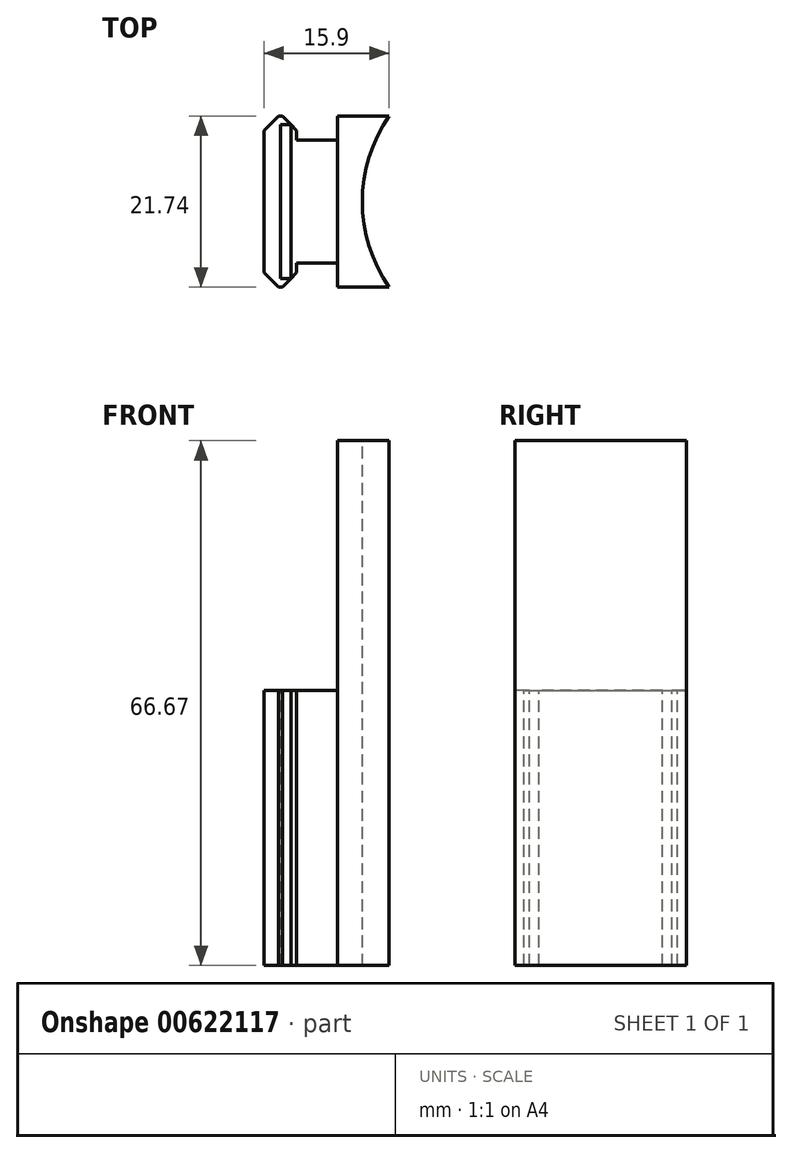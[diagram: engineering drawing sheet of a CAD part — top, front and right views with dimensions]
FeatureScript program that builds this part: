
annotation { "Feature Type Name" : "Feature", "Feature Type Description" : "" }
export const myFeature = defineFeature(function(context is Context, id is Id, definition is map)
    precondition{}
    {
        {
            var Q0;
            Q0=qCreatedBy(makeId("Top.planeOp"),FACE);
            var sketch = newSketch(context, id + "F0", { "sketchPlane" : qUnion([Q0])});
            skLineSegment(sketch, "E0", {"start": v(0, 22.6) * mm, "end": v(0, -22.6) * mm});
            skLineSegment(sketch, "E1", {"start": v(0, 0) * mm, "end": v(-7.34, 0) * mm});
            skPoint(sketch, "E1.endSnap0", {"position": v(0, 0) * mm});
            skPoint(sketch, "E2", {"position": v(-7.24, 0) * mm});
            skLineSegment(sketch, "E3.bottom", {"start": v(-9.32, -9.75) * mm, "end": v(-5.16, -9.75) * mm});
            skLineSegment(sketch, "E3.top", {"start": v(-9.32, 9.75) * mm, "end": v(-5.16, 9.75) * mm});
            skLineSegment(sketch, "E3.left", {"start": v(-9.32, -9.75) * mm, "end": v(-9.32, 9.75) * mm});
            skLineSegment(sketch, "E3.right", {"start": v(-5.16, -9.75) * mm, "end": v(-5.16, 9.75) * mm});
            skLineSegment(sketch, "E4", {"start": v(-5.16, 7.82) * mm, "end": v(0, 7.82) * mm});
            skLineSegment(sketch, "E5.MirrorCS", {"start": v(-5.16, -7.82) * mm, "end": v(0, -7.82) * mm});
            skLineSegment(sketch, "E6", {"start": v(0, 10.87) * mm, "end": v(-12.73, 10.87) * mm});
            skLineSegment(sketch, "E7.MirrorCS", {"start": v(0, -10.87) * mm, "end": v(-12.73, -10.87) * mm});
            skLineSegment(sketch, "E8", {"start": v(-7.24, -19.08) * mm, "end": v(-7.24, 22.23) * mm});
            skPoint(sketch, "E8.startSnap0", {"position": v(-7.24, -9.75) * mm});
            skLineSegment(sketch, "E9", {"start": v(-8.61, -16.87) * mm, "end": v(-8.61, 22.8) * mm});
            skLineSegment(sketch, "E10.MirrorCS", {"start": v(-5.87, -16.87) * mm, "end": v(-5.87, 22.8) * mm});
            skLineSegment(sketch, "E11", {"start": v(-8.61, 9.75) * mm, "end": v(-7.24, 11.13) * mm});
            skPoint(sketch, "E11.endSnap0", {"position": v(-6.36, -10.87) * mm});
            skLineSegment(sketch, "E12", {"start": v(-5.87, 9.75) * mm, "end": v(-7.24, 11.13) * mm});
            skLineSegment(sketch, "E13.MirrorCS", {"start": v(-8.61, -9.75) * mm, "end": v(-6.68, -11.69) * mm});
            skLineSegment(sketch, "E14.MirrorCS", {"start": v(-5.87, -9.75) * mm, "end": v(-7.24, -11.13) * mm});
            skLineSegment(sketch, "E15", {"start": v(-5.87, 9.75) * mm, "end": v(-5.16, 9.04) * mm});
            skLineSegment(sketch, "E16.MirrorCS", {"start": v(-8.61, 9.75) * mm, "end": v(-9.32, 9.04) * mm});
            skLineSegment(sketch, "E17.MirrorCS", {"start": v(-14.48, 0) * mm, "end": v(-7.14, 0) * mm});
            skLineSegment(sketch, "E18.MirrorCS", {"start": v(-8.61, -9.75) * mm, "end": v(-9.32, -9.04) * mm});
            skLineSegment(sketch, "E19.MirrorCS", {"start": v(-5.87, -9.75) * mm, "end": v(-5.16, -9.04) * mm});
            skCircle(sketch, "E20", {"center": v(22.23, 0) * mm, "radius": 19.05 * mm});
            skLineSegment(sketch, "E21", {"start": v(0, -10.87) * mm, "end": v(6.58, -10.87) * mm});
            skLineSegment(sketch, "E22", {"start": v(0, 10.87) * mm, "end": v(6.58, 10.87) * mm});
            skLineSegment(sketch, "E23", {"start": v(6.58, -10.87) * mm, "end": v(6.58, 10.87) * mm});
            skCircle(sketch, "E24", {"center": v(22.23, 0) * mm, "radius": 22.23 * mm});
            skSolve(sketch);
        }
        {
            var Q0;
            {var subQ4=sQuery(id+"F0.wireOp",EDGE,"E21");Q0=makeQuery(id+"F0.imprint","IMPRINT",FACE,{"disambiguationData":[TD([[makeQuery(id+"F0.imprint","IMPRINT",EDGE,{"derivedFrom":subQ4}),1.0]])]});}
            var Q1;
            {var subQ2=sQuery(id+"F0.wireOp",EDGE,"E22");Q1=makeQuery(id+"F0.imprint","IMPRINT",FACE,{"disambiguationData":[TD([[makeQuery(id+"F0.imprint","IMPRINT",EDGE,{"derivedFrom":subQ2}),-1.0]])]});}
            var Q2;
            {var subQ3=sQuery(id+"F0.wireOp",EDGE,"E4");Q2=makeQuery(id+"F0.imprint","IMPRINT",FACE,{"disambiguationData":[TD([[makeQuery(id+"F0.imprint","IMPRINT",EDGE,{"derivedFrom":subQ3}),-1.0]])]});}
            var Q3;
            {var subQ3=sQuery(id+"F0.wireOp",EDGE,"E5.MirrorCS");Q3=makeQuery(id+"F0.imprint","IMPRINT",FACE,{"disambiguationData":[TD([[makeQuery(id+"F0.imprint","IMPRINT",EDGE,{"derivedFrom":subQ3}),1.0]])]});}
            var Q4;
            {var subQ3=sQuery(id+"F0.wireOp",EDGE,"E1");var subQ7=sQuery(id+"F0.wireOp",EDGE,"E17.MirrorCS");var subQ9=makeQuery(id+"F0.imprint","INTERSECT",VERTEX,{"derivedFrom":[subQ3,subQ7]});Q4=makeQuery(id+"F0.imprint","IMPRINT",FACE,{"disambiguationData":[TD([[makeQuery(id+"F0.imprint","IMPRINT",EDGE,{"disambiguationData":[TD([[subQ9,1.0]])],"derivedFrom":subQ3}),1.0]])]});}
            var Q5;
            {var subQ0=sQuery(id+"F0.wireOp",EDGE,"E14.MirrorCS");var subQ5=sQuery(id+"F0.wireOp",EDGE,"E7.MirrorCS");var subQ6=makeQuery(id+"F0.imprint","INTERSECT",VERTEX,{"derivedFrom":[subQ5,subQ0]});Q5=makeQuery(id+"F0.imprint","IMPRINT",FACE,{"disambiguationData":[TD([[makeQuery(id+"F0.imprint","IMPRINT",EDGE,{"disambiguationData":[TD([[subQ6,-1.0]])],"derivedFrom":subQ5}),-1.0]])]});}
            var Q6;
            {var subQ0=sQuery(id+"F0.wireOp",EDGE,"E13.MirrorCS");var subQ5=sQuery(id+"F0.wireOp",EDGE,"E7.MirrorCS");var subQ7=makeQuery(id+"F0.imprint","INTERSECT",VERTEX,{"derivedFrom":[subQ5,subQ0]});Q6=makeQuery(id+"F0.imprint","IMPRINT",FACE,{"disambiguationData":[TD([[makeQuery(id+"F0.imprint","IMPRINT",EDGE,{"disambiguationData":[TD([[subQ7,1.0]])],"derivedFrom":subQ5}),-1.0]])]});}
            var Q7;
            {var subQ0=sQuery(id+"F0.wireOp",EDGE,"E17.MirrorCS");var subQ1=makeQuery(id+"F0.imprint","IMPRINT",VERTEX,{"derivedFrom":subQ0});Q7=makeQuery(id+"F0.imprint","IMPRINT",FACE,{"disambiguationData":[TD([[makeQuery(id+"F0.imprint","IMPRINT",EDGE,{"disambiguationData":[TD([[subQ1,1.0]])],"derivedFrom":subQ0}),-1.0]])]});}
            var Q8;
            {var subQ0=sQuery(id+"F0.wireOp",EDGE,"E19.MirrorCS");Q8=makeQuery(id+"F0.imprint","IMPRINT",FACE,{"disambiguationData":[TD([[makeQuery(id+"F0.imprint","IMPRINT",EDGE,{"derivedFrom":subQ0}),1.0]])]});}
            var Q9;
            {var subQ0=sQuery(id+"F0.wireOp",EDGE,"E15");Q9=makeQuery(id+"F0.imprint","IMPRINT",FACE,{"disambiguationData":[TD([[makeQuery(id+"F0.imprint","IMPRINT",EDGE,{"derivedFrom":subQ0}),-1.0]])]});}
            var Q10;
            {var subQ3=sQuery(id+"F0.wireOp",EDGE,"E1");var subQ7=sQuery(id+"F0.wireOp",EDGE,"E17.MirrorCS");var subQ9=makeQuery(id+"F0.imprint","INTERSECT",VERTEX,{"derivedFrom":[subQ3,subQ7]});Q10=makeQuery(id+"F0.imprint","IMPRINT",FACE,{"disambiguationData":[TD([[makeQuery(id+"F0.imprint","IMPRINT",EDGE,{"disambiguationData":[TD([[subQ9,1.0]])],"derivedFrom":subQ3}),-1.0]])]});}
            var Q11;
            {var subQ0=sQuery(id+"F0.wireOp",EDGE,"E17.MirrorCS");var subQ1=makeQuery(id+"F0.imprint","IMPRINT",VERTEX,{"derivedFrom":subQ0});Q11=makeQuery(id+"F0.imprint","IMPRINT",FACE,{"disambiguationData":[TD([[makeQuery(id+"F0.imprint","IMPRINT",EDGE,{"disambiguationData":[TD([[subQ1,1.0]])],"derivedFrom":subQ0}),1.0]])]});}
            var Q12;
            {var subQ0=sQuery(id+"F0.wireOp",EDGE,"E16.MirrorCS");Q12=makeQuery(id+"F0.imprint","IMPRINT",FACE,{"disambiguationData":[TD([[makeQuery(id+"F0.imprint","IMPRINT",EDGE,{"derivedFrom":subQ0}),1.0]])]});}
            var Q13;
            {var subQ0=sQuery(id+"F0.wireOp",EDGE,"E18.MirrorCS");Q13=makeQuery(id+"F0.imprint","IMPRINT",FACE,{"disambiguationData":[TD([[makeQuery(id+"F0.imprint","IMPRINT",EDGE,{"derivedFrom":subQ0}),-1.0]])]});}
            var Q14;
            {var subQ0=sQuery(id+"F0.wireOp",EDGE,"E12");var subQ5=sQuery(id+"F0.wireOp",EDGE,"E6");var subQ6=makeQuery(id+"F0.imprint","INTERSECT",VERTEX,{"derivedFrom":[subQ5,subQ0]});Q14=makeQuery(id+"F0.imprint","IMPRINT",FACE,{"disambiguationData":[TD([[makeQuery(id+"F0.imprint","IMPRINT",EDGE,{"disambiguationData":[TD([[subQ6,-1.0]])],"derivedFrom":subQ5}),1.0]])]});}
            var Q15;
            {var subQ0=sQuery(id+"F0.wireOp",EDGE,"E11");var subQ5=sQuery(id+"F0.wireOp",EDGE,"E6");var subQ6=makeQuery(id+"F0.imprint","INTERSECT",VERTEX,{"derivedFrom":[subQ5,subQ0]});Q15=makeQuery(id+"F0.imprint","IMPRINT",FACE,{"disambiguationData":[TD([[makeQuery(id+"F0.imprint","IMPRINT",EDGE,{"disambiguationData":[TD([[subQ6,1.0]])],"derivedFrom":subQ5}),1.0]])]});}
            var Q16;
            {var subQ0=sQuery(id+"F0.wireOp",EDGE,"E24");var subQ5=sQuery(id+"F0.wireOp",EDGE,"E21");var subQ8=makeQuery(id+"F0.imprint","INTERSECT",VERTEX,{"derivedFrom":[subQ5,subQ0]});Q16=makeQuery(id+"F0.imprint","IMPRINT",FACE,{"disambiguationData":[TD([[makeQuery(id+"F0.imprint","IMPRINT",EDGE,{"disambiguationData":[TD([[subQ8,-1.0]])],"derivedFrom":subQ5}),1.0]])]});}
            extrude(context, id + "F1", {"entities" : qUnion([Q0, Q1, Q2, Q3, Q4, Q5, Q6, Q7, Q8, Q9, Q10, Q11, Q12, Q13, Q14, Q15, Q16]), "oppositeDirection" : true, "depth" : 34.92 * mm, "offsetDistance" : 25.4 * mm});
        }
        {
            var Q0;
            {var subQ0=sQuery(id+"F0.wireOp",EDGE,"E0");var subQ1=makeQuery(id+"F0.imprint","INTERSECT",VERTEX,{"derivedFrom":[subQ0,sQuery(id+"F0.wireOp",EDGE,"E4")]});Q0=makeQuery(id+"F0.imprint","IMPRINT",FACE,{"disambiguationData":[TD([[makeQuery(id+"F0.imprint","IMPRINT",EDGE,{"disambiguationData":[TD([[subQ1,1.0]])],"derivedFrom":subQ0}),1.0]])]});}
            var Q1;
            {var subQ1=sQuery(id+"F0.wireOp",EDGE,"E0");var subQ3=makeQuery(id+"F0.imprint","INTERSECT",VERTEX,{"derivedFrom":[subQ1,sQuery(id+"F0.wireOp",EDGE,"E5.MirrorCS")]});Q1=makeQuery(id+"F0.imprint","IMPRINT",FACE,{"disambiguationData":[TD([[makeQuery(id+"F0.imprint","IMPRINT",EDGE,{"disambiguationData":[TD([[subQ3,1.0]])],"derivedFrom":subQ1}),1.0]])]});}
            var Q2;
            {var subQ0=sQuery(id+"F0.wireOp",EDGE,"E24");var subQ5=sQuery(id+"F0.wireOp",EDGE,"E21");var subQ8=makeQuery(id+"F0.imprint","INTERSECT",VERTEX,{"derivedFrom":[subQ5,subQ0]});Q2=makeQuery(id+"F0.imprint","IMPRINT",FACE,{"disambiguationData":[TD([[makeQuery(id+"F0.imprint","IMPRINT",EDGE,{"disambiguationData":[TD([[subQ8,-1.0]])],"derivedFrom":subQ5}),1.0]])]});}
            extrude(context, id + "F2", {"entities" : qUnion([Q0, Q1, Q2]), "operationType" : NewBodyOperationType.ADD, "depth" : 31.75 * mm, "offsetDistance" : 25.4 * mm});
        }
        {
            var Q0;
            Q0=makeQuery(id+"F1.opExtrude","SWEPT_BODY",BODY,{"disambiguationData":[OSD([sQuery(id+"F0.wireOp",EDGE,"E0"),sQuery(id+"F0.wireOp",EDGE,"E3.left"),sQuery(id+"F0.wireOp",EDGE,"E3.right"),sQuery(id+"F0.wireOp",EDGE,"E4"),sQuery(id+"F0.wireOp",EDGE,"E5.MirrorCS"),sQuery(id+"F0.wireOp",EDGE,"E6"),sQuery(id+"F0.wireOp",EDGE,"E7.MirrorCS"),sQuery(id+"F0.wireOp",EDGE,"E11"),sQuery(id+"F0.wireOp",EDGE,"E12"),sQuery(id+"F0.wireOp",EDGE,"E13.MirrorCS"),sQuery(id+"F0.wireOp",EDGE,"E14.MirrorCS"),sQuery(id+"F0.wireOp",EDGE,"E16.MirrorCS"),sQuery(id+"F0.wireOp",EDGE,"E15"),sQuery(id+"F0.wireOp",EDGE,"E18.MirrorCS"),sQuery(id+"F0.wireOp",EDGE,"E19.MirrorCS"),sQuery(id+"F0.wireOp",EDGE,"E20"),sQuery(id+"F0.wireOp",EDGE,"E21"),sQuery(id+"F0.wireOp",EDGE,"E22")])]});
            transform(context, id + "F3", {"entities" : qUnion([Q0]), "transformType" : TransformType.TRANSLATION_3D, "dx" : 0 * mm, "dy" : 0 * mm, "dz" : 0 * mm, "makeCopy" : true});
        }
    });
